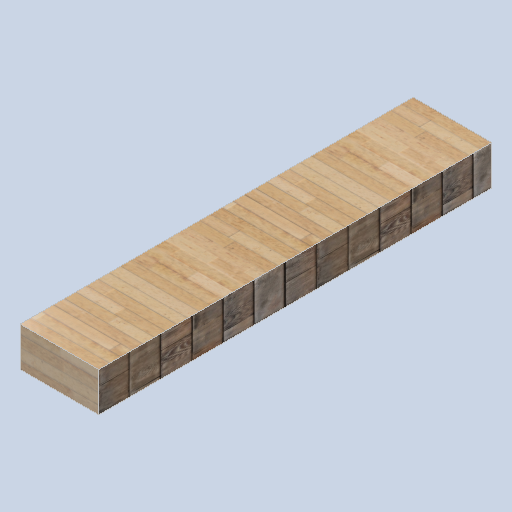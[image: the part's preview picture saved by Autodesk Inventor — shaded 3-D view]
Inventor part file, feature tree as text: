
AUTODESK INVENTOR PART (.ipt)
format: ipt  version: 2024.2 (Build 282272000, 272)  size: 218,112 bytes
history: native  units: in
note: dims shown in document units (in); Inventor stores cm internally (conversion verified against a paired STEP export)
features: other x3, sketch x1
ambient origin geometry x8: Origin, YZ Plane, XZ Plane, XY Plane, X Axis, Y Axis, Z Axis, Center Point
bodies: Solid1 (feature_tree)
feature tree (4):
  other  "support_frame_02.ipt"
  other  "Solid1::support_frame_02.ipt"
  other  "TaggingFeature1"
  sketch  "Sketch1"  dims[d0=0.3937in]
